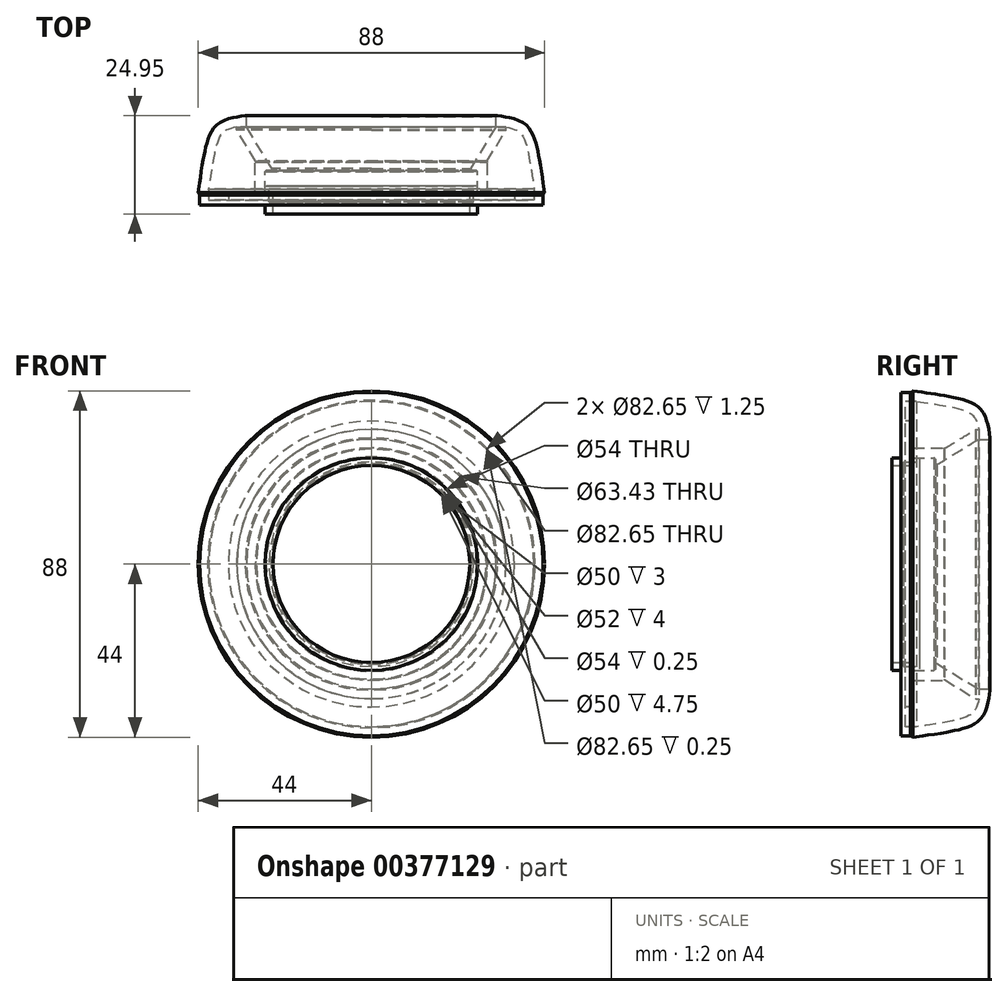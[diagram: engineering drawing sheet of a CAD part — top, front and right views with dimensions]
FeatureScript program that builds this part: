
annotation { "Feature Type Name" : "Feature", "Feature Type Description" : "" }
export const myFeature = defineFeature(function(context is Context, id is Id, definition is map)
    precondition{}
    {
        {
            var Q0;
            Q0=qCreatedBy(makeId("Right.planeOp"),FACE);
            var sketch = newSketch(context, id + "F0", { "sketchPlane" : qUnion([Q0])});
            skLineSegment(sketch, "E0", {"start": v(24.66, 0) * mm, "end": v(24.66, 44.5) * mm, "construction": true});
            skLineSegment(sketch, "E1", {"start": v(24.66, 44.5) * mm, "end": v(0, 44.5) * mm, "construction": true});
            skLineSegment(sketch, "E2.left", {"start": v(24.66, 30) * mm, "end": v(24.66, 0) * mm});
            skLineSegment(sketch, "E3.top", {"start": v(3.5, 27) * mm, "end": v(7.5, 27) * mm});
            skLineSegment(sketch, "E3.left", {"start": v(3.5, 0) * mm, "end": v(3.5, 27) * mm});
            skLineSegment(sketch, "E3.right", {"start": v(7.5, 25) * mm, "end": v(7.5, 27) * mm});
            skLineSegment(sketch, "E4", {"start": v(7.5, 25) * mm, "end": v(10, 23.5) * mm});
            skFitSpline(sketch, "E5", {"points": [v(10, 23.5) * mm, v(18.5, 0) * mm], "startDerivative": vector(10.8, -12.83) * mm, "endDerivative": vector(0.5, -36.07) * mm});
            skLineSegment(sketch, "E6", {"start": v(0, 27) * mm, "end": v(0.5, 27) * mm});
            skLineSegment(sketch, "E7", {"start": v(0.5, 27) * mm, "end": v(0.5, 0) * mm});
            skLineSegment(sketch, "E8", {"start": v(0.5, 27) * mm, "end": v(3.5, 27) * mm, "construction": true});
            skLineSegment(sketch, "E9", {"start": v(6.93, 27) * mm, "end": v(6.93, 25) * mm, "construction": true});
            skLineSegment(sketch, "E10", {"start": v(7.5, 25) * mm, "end": v(6.93, 25) * mm, "construction": true});
            skFitSpline(sketch, "E11", {"points": [v(6.93, 25) * mm, v(1.5, 0) * mm], "startDerivative": vector(-10.3, -10.3) * mm, "endDerivative": vector(-0.16, -38) * mm, "construction": true});
            skLineSegment(sketch, "E12", {"start": v(0, 27) * mm, "end": v(0, 0) * mm});
            skLineSegment(sketch, "E13", {"start": v(0, 0) * mm, "end": v(0.5, 0) * mm});
            skLineSegment(sketch, "E14.bottom", {"start": v(19.5, 32.5) * mm, "end": v(20.5, 32.5) * mm});
            skLineSegment(sketch, "E14.top", {"start": v(19.5, 0) * mm, "end": v(20.5, 0) * mm});
            skLineSegment(sketch, "E14.left", {"start": v(19.5, 32.5) * mm, "end": v(19.5, 0) * mm});
            skLineSegment(sketch, "E14.right", {"start": v(20.5, 32.5) * mm, "end": v(20.5, 0) * mm});
            skLineSegment(sketch, "E15", {"start": v(7.5, 25) * mm, "end": v(19.5, 32.5) * mm});
            skLineSegment(sketch, "E16", {"start": v(20.5, 31.72) * mm, "end": v(21.5, 31.72) * mm});
            skLineSegment(sketch, "E17", {"start": v(3.5, 0) * mm, "end": v(18.5, 0) * mm});
            skLineSegment(sketch, "E18", {"start": v(3.5, 0) * mm, "end": v(1.5, 0) * mm, "construction": true});
            skLineSegment(sketch, "E19", {"start": v(0, 44.5) * mm, "end": v(0, 27) * mm, "construction": true});
            skLineSegment(sketch, "E20", {"start": v(0, 43.65) * mm, "end": v(1.25, 43.65) * mm, "construction": true});
            skLineSegment(sketch, "E21", {"start": v(1.25, 43.65) * mm, "end": v(1.25, 39) * mm});
            skLineSegment(sketch, "E22", {"start": v(1.25, 39) * mm, "end": v(0, 39) * mm, "construction": true});
            skLineSegment(sketch, "E23", {"start": v(1.25, 43.65) * mm, "end": v(1.75, 43.65) * mm, "construction": true});
            skLineSegment(sketch, "E24", {"start": v(1.75, 43.65) * mm, "end": v(1.75, 39) * mm, "construction": true});
            skLineSegment(sketch, "E25", {"start": v(1.75, 39) * mm, "end": v(1.25, 39) * mm});
            skLineSegment(sketch, "E26", {"start": v(1.5, 43.65) * mm, "end": v(1.85, 44) * mm});
            skFitSpline(sketch, "E27", {"points": [v(1.85, 44) * mm, v(21.5, 31.72) * mm], "startDerivative": vector(27.86, -4.33) * mm, "endDerivative": vector(7.5, -23.03) * mm});
            skLineSegment(sketch, "E28", {"start": v(1.5, 43.65) * mm, "end": v(1.75, 43.65) * mm});
            skFitSpline(sketch, "E29.0", {"points": [v(1.55, 42.02) * mm, v(3.8, 41.67) * mm, v(8.1, 40.77) * mm, v(12.58, 38.96) * mm, v(15.46, 37.06) * mm, v(17.25, 35.4) * mm, v(18.65, 33.45) * mm, v(19.33, 31.93) * mm, v(19.6, 31.1) * mm]});
            skLineSegment(sketch, "E30", {"start": v(1.75, 43.65) * mm, "end": v(1.75, 42) * mm});
            skLineSegment(sketch, "E31.0", {"start": v(10.13, 29) * mm, "end": v(18.19, 34.04) * mm});
            skLineSegment(sketch, "E32", {"start": v(1.75, 39) * mm, "end": v(1.75, 27) * mm, "construction": true});
            skLineSegment(sketch, "E33", {"start": v(1.75, 29) * mm, "end": v(10.13, 29) * mm});
            skLineSegment(sketch, "E34", {"start": v(1.75, 29) * mm, "end": v(1.75, 27) * mm});
            skLineSegment(sketch, "E35", {"start": v(1.75, 27) * mm, "end": v(3.5, 27) * mm});
            skLineSegment(sketch, "E36", {"start": v(0.5, 0) * mm, "end": v(-42.58, 0) * mm, "construction": true});
            skLineSegment(sketch, "E37", {"start": v(1.25, 39) * mm, "end": v(1.75, 39) * mm});
            skLineSegment(sketch, "E38", {"start": v(1.25, 43.65) * mm, "end": v(-1.25, 43.65) * mm});
            skLineSegment(sketch, "E39", {"start": v(1.75, 39) * mm, "end": v(1.75, 27) * mm});
            skLineSegment(sketch, "E40", {"start": v(3.5, 25) * mm, "end": v(0.5, 25) * mm});
            skLineSegment(sketch, "E41", {"start": v(0.5, 25) * mm, "end": v(0.5, 27) * mm});
            skLineSegment(sketch, "E42", {"start": v(0.5, 27) * mm, "end": v(-0.5, 27) * mm});
            skLineSegment(sketch, "E43", {"start": v(-1.25, 43.65) * mm, "end": v(-1.25, 39) * mm});
            skLineSegment(sketch, "E44", {"start": v(-1.25, 39) * mm, "end": v(-0.5, 39) * mm});
            skLineSegment(sketch, "E45", {"start": v(-0.5, 39) * mm, "end": v(-0.5, 27) * mm});
            skLineSegment(sketch, "E46", {"start": v(-0.5, 39) * mm, "end": v(0, 39) * mm, "construction": true});
            skLineSegment(sketch, "E47", {"start": v(0, 26.41) * mm, "end": v(0.5, 26.41) * mm, "construction": true});
            skLineSegment(sketch, "E48", {"start": v(-0.5, 27.32) * mm, "end": v(0, 27.32) * mm, "construction": true});
            skLineSegment(sketch, "E49.bottom", {"start": v(1.25, 43.65) * mm, "end": v(1.75, 43.65) * mm});
            skLineSegment(sketch, "E49.right", {"start": v(1.75, 43.65) * mm, "end": v(1.75, 39) * mm});
            skLineSegment(sketch, "E50", {"start": v(-0.5, 39) * mm, "end": v(-1.75, 39) * mm});
            skLineSegment(sketch, "E51", {"start": v(-1.75, 39) * mm, "end": v(-1.75, 27) * mm});
            skLineSegment(sketch, "E52", {"start": v(-1.75, 27) * mm, "end": v(-3.5, 27) * mm});
            skLineSegment(sketch, "E53", {"start": v(-3.5, 27) * mm, "end": v(-3.5, 25) * mm});
            skLineSegment(sketch, "E54", {"start": v(-3.5, 25) * mm, "end": v(-0.5, 25) * mm});
            skLineSegment(sketch, "E55", {"start": v(-0.5, 25) * mm, "end": v(-0.5, 27) * mm});
            skLineSegment(sketch, "E56", {"start": v(0, 29.76) * mm, "end": v(1.75, 29.76) * mm, "construction": true});
            skLineSegment(sketch, "E57", {"start": v(0, 29.05) * mm, "end": v(-1.75, 29.05) * mm, "construction": true});
            skLineSegment(sketch, "E58", {"start": v(-1.75, 27) * mm, "end": v(-0.5, 27) * mm, "construction": true});
            skLineSegment(sketch, "E59", {"start": v(-0.5, 25) * mm, "end": v(0.5, 25) * mm, "construction": true});
            skLineSegment(sketch, "E60.bottom", {"start": v(-0.5, 27) * mm, "end": v(-1, 27) * mm});
            skLineSegment(sketch, "E60.top", {"start": v(-0.5, 25) * mm, "end": v(-1, 25) * mm});
            skLineSegment(sketch, "E60.left", {"start": v(-0.5, 27) * mm, "end": v(-0.5, 25) * mm});
            skLineSegment(sketch, "E60.right", {"start": v(-1, 27) * mm, "end": v(-1, 25) * mm});
            skLineSegment(sketch, "E61.bottom", {"start": v(0.5, 27) * mm, "end": v(1, 27) * mm});
            skLineSegment(sketch, "E61.top", {"start": v(0.5, 25) * mm, "end": v(1, 25) * mm});
            skLineSegment(sketch, "E61.left", {"start": v(0.5, 27) * mm, "end": v(0.5, 25) * mm});
            skLineSegment(sketch, "E61.right", {"start": v(1, 27) * mm, "end": v(1, 25) * mm});
            skLineSegment(sketch, "E62", {"start": v(0.5, 26) * mm, "end": v(1, 26) * mm, "construction": true});
            skLineSegment(sketch, "E63", {"start": v(-0.5, 26) * mm, "end": v(-1, 26) * mm, "construction": true});
            skSolve(sketch);
        }
        {
            var Q0;
            Q0=qCreatedBy(makeId("Right.planeOp"),FACE);
            var sketch = newSketch(context, id + "F1", { "sketchPlane" : qUnion([Q0])});
            skLineSegment(sketch, "E64", {"start": v(1.25, 43.65) * mm, "end": v(1.25, 27) * mm});
            skLineSegment(sketch, "E65", {"start": v(1.25, 27) * mm, "end": v(3.5, 27) * mm});
            skLineSegment(sketch, "E66", {"start": v(3.5, 27) * mm, "end": v(3.5, 26) * mm});
            skLineSegment(sketch, "E67", {"start": v(1.25, 43.65) * mm, "end": v(-1.25, 43.65) * mm});
            skLineSegment(sketch, "E68", {"start": v(-1.25, 43.65) * mm, "end": v(-1.25, 27) * mm});
            skLineSegment(sketch, "E69", {"start": v(-1.25, 27) * mm, "end": v(-3.5, 27) * mm});
            skLineSegment(sketch, "E70", {"start": v(-3.5, 27) * mm, "end": v(-3.5, 25) * mm});
            skLineSegment(sketch, "E71", {"start": v(-3.5, 25) * mm, "end": v(-0.5, 25) * mm});
            skLineSegment(sketch, "E72", {"start": v(-0.5, 25) * mm, "end": v(-0.5, 26) * mm});
            skLineSegment(sketch, "E73", {"start": v(-0.5, 26) * mm, "end": v(3.5, 26) * mm});
            skLineSegment(sketch, "E74", {"start": v(0, 42.6) * mm, "end": v(1.25, 42.6) * mm, "construction": true});
            skLineSegment(sketch, "E75", {"start": v(0, 42.06) * mm, "end": v(-1.25, 42.06) * mm, "construction": true});
            skFitSpline(sketch, "E76.0", {"points": [v(1.85, 44) * mm, v(11.14, 42.56) * mm, v(19, 39.4) * mm, v(21.5, 31.72) * mm]});
            skLineSegment(sketch, "E77", {"start": v(1.85, 44) * mm, "end": v(1.5, 43.65) * mm});
            skLineSegment(sketch, "E78", {"start": v(1.5, 43.65) * mm, "end": v(1.5, 27) * mm});
            skLineSegment(sketch, "E79", {"start": v(1.5, 27) * mm, "end": v(7.5, 27) * mm});
            skLineSegment(sketch, "E80", {"start": v(21.5, 31.72) * mm, "end": v(18.5, 31.72) * mm});
            skLineSegment(sketch, "E81", {"start": v(18.5, 31.72) * mm, "end": v(7.5, 25) * mm});
            skLineSegment(sketch, "E82", {"start": v(7.5, 25) * mm, "end": v(7.5, 27) * mm});
            skLineSegment(sketch, "E83.bottom", {"start": v(1.25, 43.65) * mm, "end": v(1.5, 43.65) * mm});
            skLineSegment(sketch, "E83.top", {"start": v(1.25, 27) * mm, "end": v(1.5, 27) * mm});
            skLineSegment(sketch, "E84.bottom", {"start": v(18.5, 31.72) * mm, "end": v(20.5, 31.72) * mm});
            skLineSegment(sketch, "E84.top", {"start": v(18.5, 0) * mm, "end": v(20.5, 0) * mm});
            skLineSegment(sketch, "E84.left", {"start": v(18.5, 31.72) * mm, "end": v(18.5, 0) * mm});
            skLineSegment(sketch, "E84.right", {"start": v(20.5, 31.72) * mm, "end": v(20.5, 0) * mm});
            skLineSegment(sketch, "E85", {"start": v(0, 0) * mm, "end": v(-10.97, 0) * mm});
            skSolve(sketch);
        }
        {
            var Q0;
            Q0=qCreatedBy(makeId("Right.planeOp"),FACE);
            var sketch = newSketch(context, id + "F2", { "sketchPlane" : qUnion([Q0])});
            skLineSegment(sketch, "E86", {"start": v(-1.25, 43.65) * mm, "end": v(1.25, 43.65) * mm});
            skLineSegment(sketch, "E87", {"start": v(1.25, 43.65) * mm, "end": v(1.25, 27) * mm});
            skLineSegment(sketch, "E88", {"start": v(1.25, 27) * mm, "end": v(3.5, 27) * mm});
            skLineSegment(sketch, "E89", {"start": v(3.5, 27) * mm, "end": v(3.5, 25) * mm});
            skLineSegment(sketch, "E90", {"start": v(3.5, 25) * mm, "end": v(-1.25, 25) * mm});
            skLineSegment(sketch, "E91", {"start": v(-1.25, 25) * mm, "end": v(-1.25, 43.65) * mm});
            skSolve(sketch);
        }
        {
            var Q0;
            {var subQ1=sQuery(id+"F1.wireOp",EDGE,"E66");Q0=makeQuery(id+"F1.imprint","IMPRINT",FACE,{"disambiguationData":[TD([[makeQuery(id+"F1.imprint","IMPRINT",EDGE,{"derivedFrom":subQ1}),-1.0]])]});}
            var Q1;
            Q1=sQuery(id+"F1.wireOp",EDGE,"E85");
            revolve(context, id + "F3", {"entities" : qUnion([Q0]), "axis" : qUnion([Q1]), "revolveType" : RevolveType.FULL});
        }
        {
            var Q0;
            Q0=makeQuery(id+"F1.imprint","IMPRINT",FACE,{"disambiguationData":[TD([[makeQuery(id+"F1.imprint","IMPRINT",EDGE,{"derivedFrom":sQuery(id+"F1.wireOp",EDGE,"E84.bottom")}),-1.0]])]});
            var Q1;
            Q1=makeQuery(id+"F1.imprint","IMPRINT",FACE,{"disambiguationData":[TD([[makeQuery(id+"F1.imprint","IMPRINT",EDGE,{"derivedFrom":sQuery(id+"F1.wireOp",EDGE,"E83.bottom")}),-1.0]])]});
            var Q2;
            Q2=sQuery(id+"F1.wireOp",EDGE,"E85");
            revolve(context, id + "F4", {"entities" : qUnion([Q0, Q1]), "axis" : qUnion([Q2]), "revolveType" : RevolveType.FULL});
        }
        {
            var Q0;
            Q0=makeQuery(id+"F1.imprint","IMPRINT",FACE,{"disambiguationData":[TD([[makeQuery(id+"F1.imprint","IMPRINT",EDGE,{"derivedFrom":sQuery(id+"F1.wireOp",EDGE,"E76.0")}),-1.0]])]});
            var Q1;
            Q1=sQuery(id+"F1.wireOp",EDGE,"E85");
            revolve(context, id + "F5", {"entities" : qUnion([Q0]), "axis" : qUnion([Q1]), "revolveType" : RevolveType.FULL});
        }
        {
            var Q0;
            Q0=makeQuery(id+"F2.imprint","IMPRINT",FACE,{"disambiguationData":[TD([[makeQuery(id+"F2.imprint","IMPRINT",EDGE,{"derivedFrom":sQuery(id+"F2.wireOp",EDGE,"E86")}),-1.0]])]});
            var Q1;
            Q1=sQuery(id+"F1.wireOp",EDGE,"E85");
            revolve(context, id + "F6", {"entities" : qUnion([Q0]), "axis" : qUnion([Q1]), "revolveType" : RevolveType.FULL});
        }
        {
            var Q0;
            Q0=makeQuery(id+"F5.opRevolve","SWEPT_FACE",FACE,{"disambiguationData":[OSD([sQuery(id+"F1.wireOp",EDGE,"E78")])]});
            shell(context, id + "F7", {"entities" : qUnion([Q0]), "thickness" : 2.5 * mm});
        }
        {
            var Q0;
            Q0=qCreatedBy(makeId("Front.planeOp"),FACE);
            var sketch = newSketch(context, id + "F8", { "sketchPlane" : qUnion([Q0])});
            skCircle(sketch, "E92.0", {"center": v(0, 0) * mm, "radius": 41.32 * mm});
            skCircle(sketch, "E93.0", {"center": v(0, 0) * mm, "radius": 36.32 * mm});
            skSolve(sketch);
        }
        {
            var Q0;
            Q0 = qSketchRegion(id + "F8", true);
            extrude(context, id + "F9", {"entities" : qUnion([Q0]), "operationType" : NewBodyOperationType.REMOVE, "oppositeDirection" : true, "depth" : 2.75 * mm});
        }
        {
            var Q0;
            Q0=makeQuery(id+"F5.opRevolve","SWEPT_EDGE",EDGE,{"disambiguationData":[OSD([sQuery(id+"F1.wireOp",EDGE,"E76.0"),sQuery(id+"F1.wireOp",EDGE,"E80")])]});
            var Q1;
            Q1=makeQuery(id+"F5.opRevolve","SWEPT_EDGE",EDGE,{"disambiguationData":[OSD([sQuery(id+"F1.wireOp",EDGE,"E81"),sQuery(id+"F1.wireOp",EDGE,"E82")])]});
            var Q2;
            Q2=makeQuery(id+"F9.boolean.opBoolean","INTERSECT",EDGE,{"derivedFrom":[makeQuery(id+"F5.opRevolve","SWEPT_FACE",FACE,{"disambiguationData":[OSD([sQuery(id+"F1.wireOp",EDGE,"E78")])]}),makeQuery(id+"F9.opExtrude","SWEPT_FACE",FACE,{"disambiguationData":[OSD([sQuery(id+"F8.wireOp",EDGE,"E92.0")])]})]});
            var Q3;
            Q3=makeQuery(id+"F7.opShell","OFFSET_EDGE",EDGE,{"disambiguationData":[OSD([sQuery(id+"F1.wireOp",EDGE,"E79"),sQuery(id+"F1.wireOp",EDGE,"E83.top"),sQuery(id+"F1.wireOp",EDGE,"E78")])]});
            var Q4;
            Q4=makeQuery(id+"F5.opRevolve","SWEPT_EDGE",EDGE,{"disambiguationData":[OSD([sQuery(id+"F1.wireOp",EDGE,"E79"),sQuery(id+"F1.wireOp",EDGE,"E83.top"),sQuery(id+"F1.wireOp",EDGE,"E78")])]});
            var Q5;
            Q5=makeQuery(id+"F7.opShell","OFFSET_EDGE",EDGE,{"disambiguationData":[OSD([sQuery(id+"F1.wireOp",EDGE,"E81"),sQuery(id+"F1.wireOp",EDGE,"E84.bottom"),sQuery(id+"F1.wireOp",EDGE,"E84.left")])]});
            chamfer(context, id + "F10", {"entities" : qUnion([Q0, Q1, Q2, Q3, Q4, Q5]), "width" : 0.3 * mm, "tangentPropagation" : true});
        }
    });
